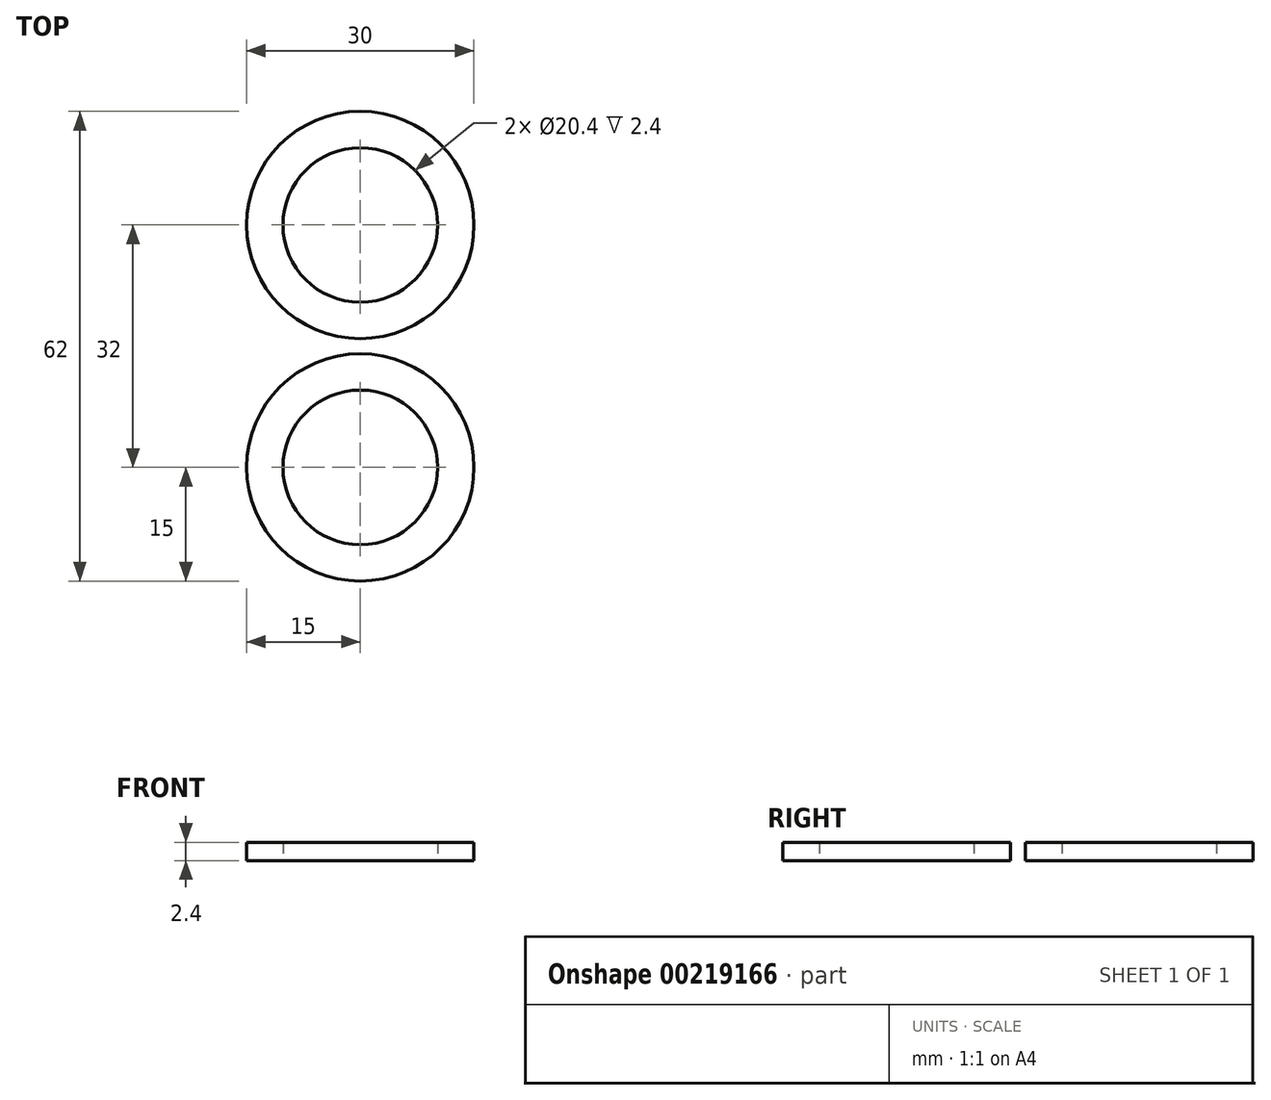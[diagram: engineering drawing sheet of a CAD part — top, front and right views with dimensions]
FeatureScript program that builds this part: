
annotation { "Feature Type Name" : "Feature", "Feature Type Description" : "" }
export const myFeature = defineFeature(function(context is Context, id is Id, definition is map)
    precondition{}
    {
        {
            var Q0;
            Q0=qCreatedBy(makeId("Top.planeOp"),FACE);
            var sketch = newSketch(context, id + "F0", { "sketchPlane" : qUnion([Q0])});
            skCircle(sketch, "E0", {"center": v(0, 0) * mm, "radius": 10.2 * mm});
            skCircle(sketch, "E1", {"center": v(0, 0) * mm, "radius": 15 * mm});
            skCircle(sketch, "E2.0.1.0", {"center": v(0, 32) * mm, "radius": 15 * mm});
            skCircle(sketch, "E2.0.1.1", {"center": v(0, 32) * mm, "radius": 10.2 * mm});
            skLineSegment(sketch, "E2.direction1", {"start": v(0, 0) * mm, "end": v(32, 0) * mm, "construction": true});
            skLineSegment(sketch, "E2.direction2", {"start": v(0, 0) * mm, "end": v(0, 32) * mm, "construction": true});
            skSolve(sketch);
        }
        {
            var Q0;
            Q0=makeQuery(id+"F0.imprint","IMPRINT",FACE,{"disambiguationData":[TD([[makeQuery(id+"F0.imprint","IMPRINT",EDGE,{"derivedFrom":sQuery(id+"F0.wireOp",EDGE,"E2.0.1.0")}),1.0]])]});
            var Q1;
            Q1=makeQuery(id+"F0.imprint","IMPRINT",FACE,{"disambiguationData":[TD([[makeQuery(id+"F0.imprint","IMPRINT",EDGE,{"derivedFrom":sQuery(id+"F0.wireOp",EDGE,"E2.1.1.0")}),1.0]])]});
            var Q2;
            Q2=makeQuery(id+"F0.imprint","IMPRINT",FACE,{"disambiguationData":[TD([[makeQuery(id+"F0.imprint","IMPRINT",EDGE,{"derivedFrom":sQuery(id+"F0.wireOp",EDGE,"E2.1.0.0")}),1.0]])]});
            var Q3;
            Q3=makeQuery(id+"F0.imprint","IMPRINT",FACE,{"disambiguationData":[TD([[makeQuery(id+"F0.imprint","IMPRINT",EDGE,{"derivedFrom":sQuery(id+"F0.wireOp",EDGE,"E0")}),-1.0]])]});
            extrude(context, id + "F1", {"entities" : qUnion([Q0, Q1, Q2, Q3]), "depth" : 2.4 * mm});
        }
    });
